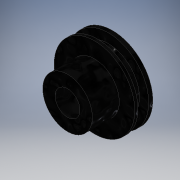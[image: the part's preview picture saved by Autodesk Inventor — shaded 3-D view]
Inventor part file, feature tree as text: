
AUTODESK INVENTOR PART (.ipt)
format: ipt  version: 2019.4 (Build 234330000, 330)  size: 311,296 bytes
history: native  units: mm
features: sketch x8, extrude x7, pattern_circular x3, projected_geometry x3, fillet x2, hole x1
ambient origin geometry x8: Origin, YZ Plane, XZ Plane, XY Plane, X Axis, Y Axis, Z Axis, Center Point
bodies: Solid1 (feature_tree)
feature tree (24):
  extrude  "Extrusion1"  Depth=12.0mm
  extrude  "Extrusion2"  Depth=3.0mm TaperAngle=0.0deg
  extrude  "Extrusion3"  Depth=1.5mm TaperAngle=0.0deg
  extrude  "Extrusion4"  Depth=5.2mm TaperAngle=0.0deg
  extrude  "Extrusion5"  Depth=2.0mm
  extrude  "Extrusion6"  Depth=1.8mm
  fillet  "Fillet1"  Radius=0.9mm
  pattern_circular  "Circular Pattern1"  Count=4 Angle=360.0deg
  hole  "Hole1"  [1 undecoded]
  pattern_circular  "Circular Pattern2"  Count=4 Angle=360.0deg
  extrude  "Extrusion7"  Depth=3.0mm
  fillet  "Fillet2"  Radius=40.0mm
  pattern_circular  "Circular Pattern3"  [2 undecoded]
  sketch  "Sketch1"  dims[d0=24.0mm d1=12.0mm]
  sketch  "Sketch2"  dims[d2=10.0mm d3=0.0mm d4=3.0mm d5=0.0mm]
  projected_geometry  "Projected Loop1"
  sketch  "Sketch3"  dims[d6=39.0mm d7=1.5mm d8=0.0mm]
  sketch  "Sketch4"  dims[d9=30.0mm d10=5.2mm d11=0.0mm]
  projected_geometry  "Projected Loop2"
  sketch  "Sketch5"  dims[d12=2.0mm d13=0.0mm d14=14.2mm]
  sketch  "Sketch6"  dims[d15=21.2mm d16=1.8mm d17=0.9mm d18=40.0mm d20=360.0deg]
  sketch  "Sketch7"  dims[d22=7.0mm d23=0.0mm d24=1.7mm d25=40.0mm d26=360.0deg]
  sketch  "Sketch8"  dims[d28=25.0mm d29=3.0mm d30=2.459mm d31=6.0mm d32=4.0mm d33=2.0mm d34=90.0deg d35=8.0mm d36=0.0mm d37=40.0mm d38=360.0deg d40=25.0mm d41=36.0mm d42=7.3mm d43=3.65mm d44=40.0mm d46=360.0deg d48=2.0mm d49=0.0mm d50=2.6mm d51=40.0mm d52=360.0deg]
  projected_geometry  "Projected Loop3"
note: 3 required parameter values undecoded (feature->parameter linkage not recoverable at this tier; creation-order binding heuristic only, values carry confidence <= 0.55)
